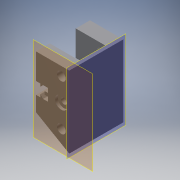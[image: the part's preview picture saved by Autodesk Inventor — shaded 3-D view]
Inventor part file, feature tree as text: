
AUTODESK INVENTOR PART (.ipt)
format: ipt  version: 2016 (Build 200138000, 138)  size: 229,376 bytes
history: native  units: in
note: dims shown in document units (in); Inventor stores cm internally (conversion verified against a paired STEP export)
features: sketch x9, extrude x9, projected_geometry x6, plane x4, reference x1
ambient origin geometry x8: Origin, YZ Plane, XZ Plane, XY Plane, X Axis, Y Axis, Z Axis, Center Point
bodies: Solid1 (feature_tree)
feature tree (29):
  plane  "Work Plane1"
  plane  "Work Plane2"
  sketch  "Sketch1"  dims[d0=60.0deg d1=1.0in d2=0.0in]
  plane  "Work Plane3"
  extrude  "Extrusion1"  Depth=1.0in TaperAngle=0.0deg
  extrude  "Extrusion2"  Depth=0.6299in
  extrude  "Extrusion3"  Depth=0.4331in
  extrude  "Extrusion4"  Depth=0.9055in
  sketch  "Sketch5"  dims[d11=0.1969in d12=0.0in d13=0.5in]
  plane  "Work Plane4"
  extrude  "Extrusion5"  Depth=0.1969in
  extrude  "Extrusion6"  Depth=0.2756in TaperAngle=0.0deg
  extrude  "Extrusion7"  Depth=0.8661in
  extrude  "Extrusion8"  Depth=0.1181in
  extrude  "Extrusion9"  Depth=0.2362in
  reference  "Reference1"
  sketch  "Sketch2"  dims[d3=2.4375in d4=0.0in d5=0.6299in]
  sketch  "Sketch3"  dims[d6=0.6299in d7=0.4331in]
  projected_geometry  "Projected Loop1"
  sketch  "Sketch4"  dims[d8=8.9375in d9=0.0in d10=0.9055in]
  projected_geometry  "Projected Loop2"
  sketch  "Sketch6"  dims[d14=0.1969in d15=0.0in d16=0.2756in d17=0.0in]
  projected_geometry  "Projected Loop3"
  sketch  "Sketch7"  dims[d18=0.8661in d19=0.8661in]
  projected_geometry  "Projected Loop4"
  sketch  "Sketch8"  dims[d20=20.0in d21=0.0in d22=0.1181in]
  projected_geometry  "Projected Loop5"
  sketch  "Sketch10"  dims[d23=0.2362in d24=0.2362in d25=0.1181in d26=0.1969in d27=0.1969in d28=20.0in d29=0.0in d32=20.0in d33=0.0in]
  projected_geometry  "Projected Loop7"
